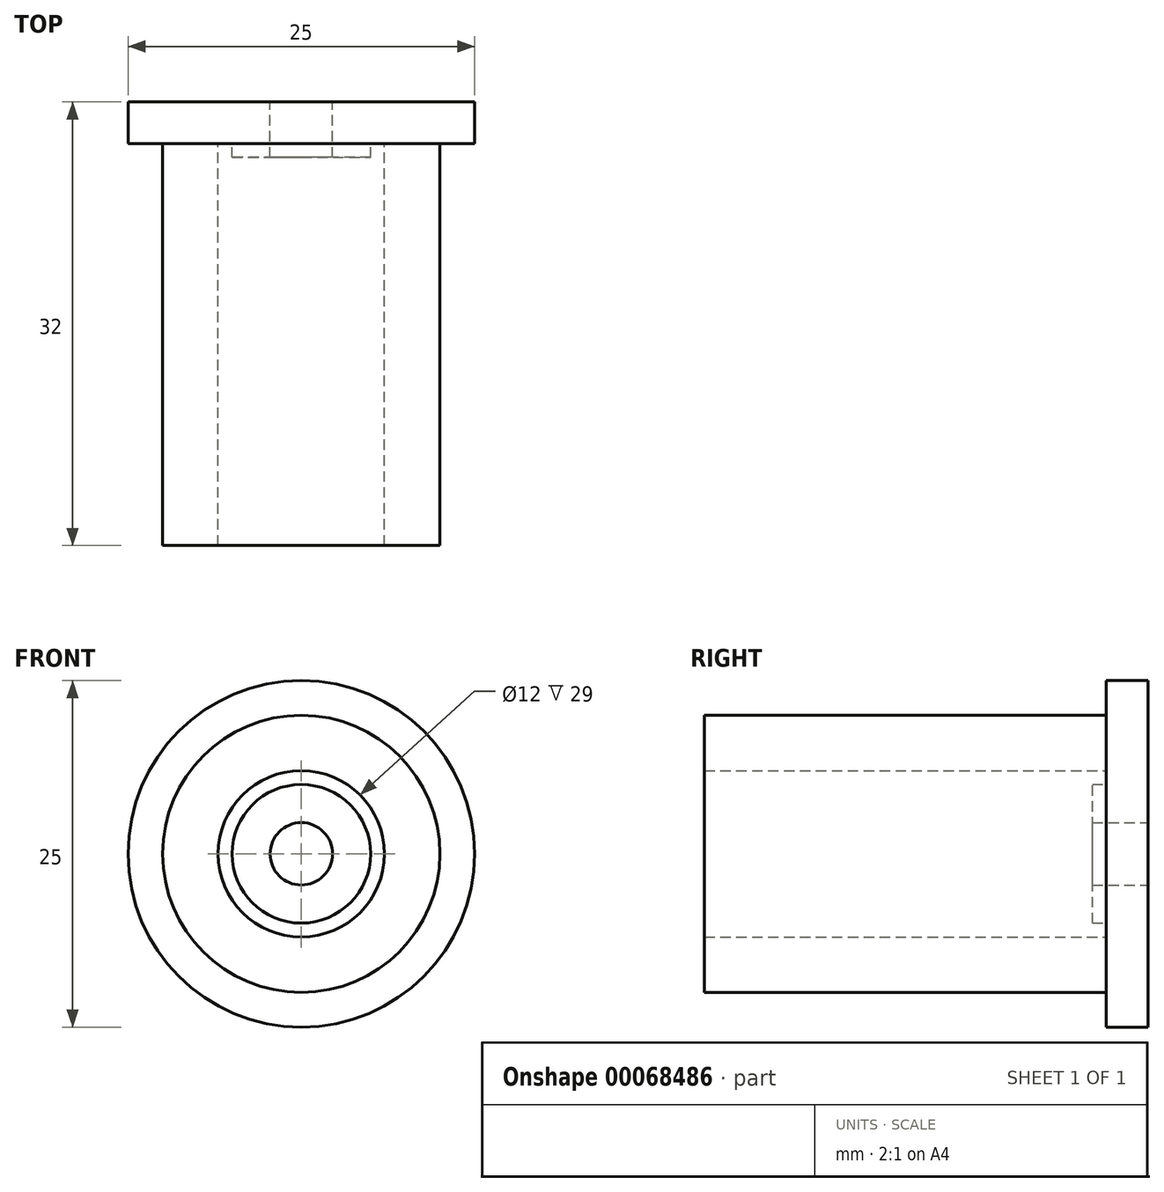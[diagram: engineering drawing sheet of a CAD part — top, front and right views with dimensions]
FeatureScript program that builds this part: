
annotation { "Feature Type Name" : "Feature", "Feature Type Description" : "" }
export const myFeature = defineFeature(function(context is Context, id is Id, definition is map)
    precondition{}
    {
        {
            var Q0;
            Q0=qCreatedBy(makeId("Front.planeOp"),FACE);
            var sketch = newSketch(context, id + "F0", { "sketchPlane" : qUnion([Q0])});
            skCircle(sketch, "E0", {"center": v(0, 0) * mm, "radius": 5 * mm});
            skCircle(sketch, "E1", {"center": v(0, 0) * mm, "radius": 10 * mm});
            skCircle(sketch, "E2", {"center": v(0, 0) * mm, "radius": 6 * mm});
            skCircle(sketch, "E3", {"center": v(0, 0) * mm, "radius": 12.5 * mm});
            skCircle(sketch, "E4", {"center": v(0, 0) * mm, "radius": 2.25 * mm});
            skSolve(sketch);
        }
        {
            var Q0;
            Q0=makeQuery(id+"F0.imprint","IMPRINT",FACE,{"disambiguationData":[TD([[makeQuery(id+"F0.imprint","IMPRINT",EDGE,{"derivedFrom":sQuery(id+"F0.wireOp",EDGE,"E0")}),1.0]])]});
            var Q1;
            Q1=makeQuery(id+"F0.imprint","IMPRINT",FACE,{"disambiguationData":[TD([[makeQuery(id+"F0.imprint","IMPRINT",EDGE,{"derivedFrom":sQuery(id+"F0.wireOp",EDGE,"E1")}),1.0]])]});
            var Q2;
            Q2=makeQuery(id+"F0.imprint","IMPRINT",FACE,{"disambiguationData":[TD([[makeQuery(id+"F0.imprint","IMPRINT",EDGE,{"derivedFrom":sQuery(id+"F0.wireOp",EDGE,"E0")}),-1.0]])]});
            var Q3;
            Q3=makeQuery(id+"F0.imprint","IMPRINT",FACE,{"disambiguationData":[TD([[makeQuery(id+"F0.imprint","IMPRINT",EDGE,{"derivedFrom":sQuery(id+"F0.wireOp",EDGE,"E1")}),-1.0]])]});
            extrude(context, id + "F1", {"entities" : qUnion([Q0, Q1, Q2, Q3]), "flatOperationType" : FlatOperationType.REMOVE, "offsetDistance" : 25 * mm, "depth" : 3 * mm, "domain" : OperationDomain.MODEL});
        }
        {
            var Q0;
            Q0=makeQuery(id+"F0.imprint","IMPRINT",FACE,{"disambiguationData":[TD([[makeQuery(id+"F0.imprint","IMPRINT",EDGE,{"derivedFrom":sQuery(id+"F0.wireOp",EDGE,"E0")}),1.0]])]});
            extrude(context, id + "F2", {"entities" : qUnion([Q0]), "operationType" : NewBodyOperationType.ADD, "flatOperationType" : FlatOperationType.REMOVE, "offsetDistance" : 25 * mm, "depth" : 4 * mm, "domain" : OperationDomain.MODEL});
        }
        {
            var Q0;
            Q0=makeQuery(id+"F0.imprint","IMPRINT",FACE,{"disambiguationData":[TD([[makeQuery(id+"F0.imprint","IMPRINT",EDGE,{"derivedFrom":sQuery(id+"F0.wireOp",EDGE,"E1")}),1.0]])]});
            extrude(context, id + "F3", {"entities" : qUnion([Q0]), "operationType" : NewBodyOperationType.ADD, "flatOperationType" : FlatOperationType.REMOVE, "offsetDistance" : 25 * mm, "depth" : 32 * mm, "domain" : OperationDomain.MODEL});
        }
    });
